# Revit family: PROOX Toilet brush holder EN
name_source: partatom
category: Furniture
revit_build: Autodesk Revit 2014 (Build: 20130308_1515(x64)
units: mm (PartAtom-declared; Revit-internal decimal feet)

## types (2) — shared parameters
BIM objects producer = www.BIMtelligent.eu
Manufacturer = PROOX Ltd.
Product data sheet = http://www.proox.com
URL = http://www.proox.com

## per-type parameters (varying)
| type | Cost | Description | EAN-No. | Material | Model | Specification |
| ONE pure | 136 $ | toilet brush holder PROOX ONE pure made from stainless steel | 9120050350137 | PROOX Stainless steel, brushed | PU-500 | Toilet brush holder made out of stainless steel. Surface with fine brushed structure. Cover 1.5 mm thickness, closed all around. Intended for wall mounting. Perforated designed area with 4mm drillings. Including plastic bin for easy cleaning. Brush handle made out of stainless steel. Brush head stays in dry area. Including stainless steel screws and anchors. |
| ONE dark passion | 152 $ | toilet brush holder PROOX ONE dark passion made from aluminum black anodized | 9120050350250 | PROOX Aluminum, black anodised | DP-500 | Toilet brush holder made out from glass pearl blasted and black anodised aluminum. Cover 3 mm thickness, closed all around. Intended for wall mounting. Perforated designed area with 4mm drillings. Including plastic bin for easy cleaning. Brush handle made out of stainless steel. Brush head stays in dry area. Including stainless steel screws and anchors. |

note: column(s) folded — value = type name in every type: Type Comments

## geometry (parser evidence)
native form markers: Sweep x1
no freeform markers — native parametric forms only
